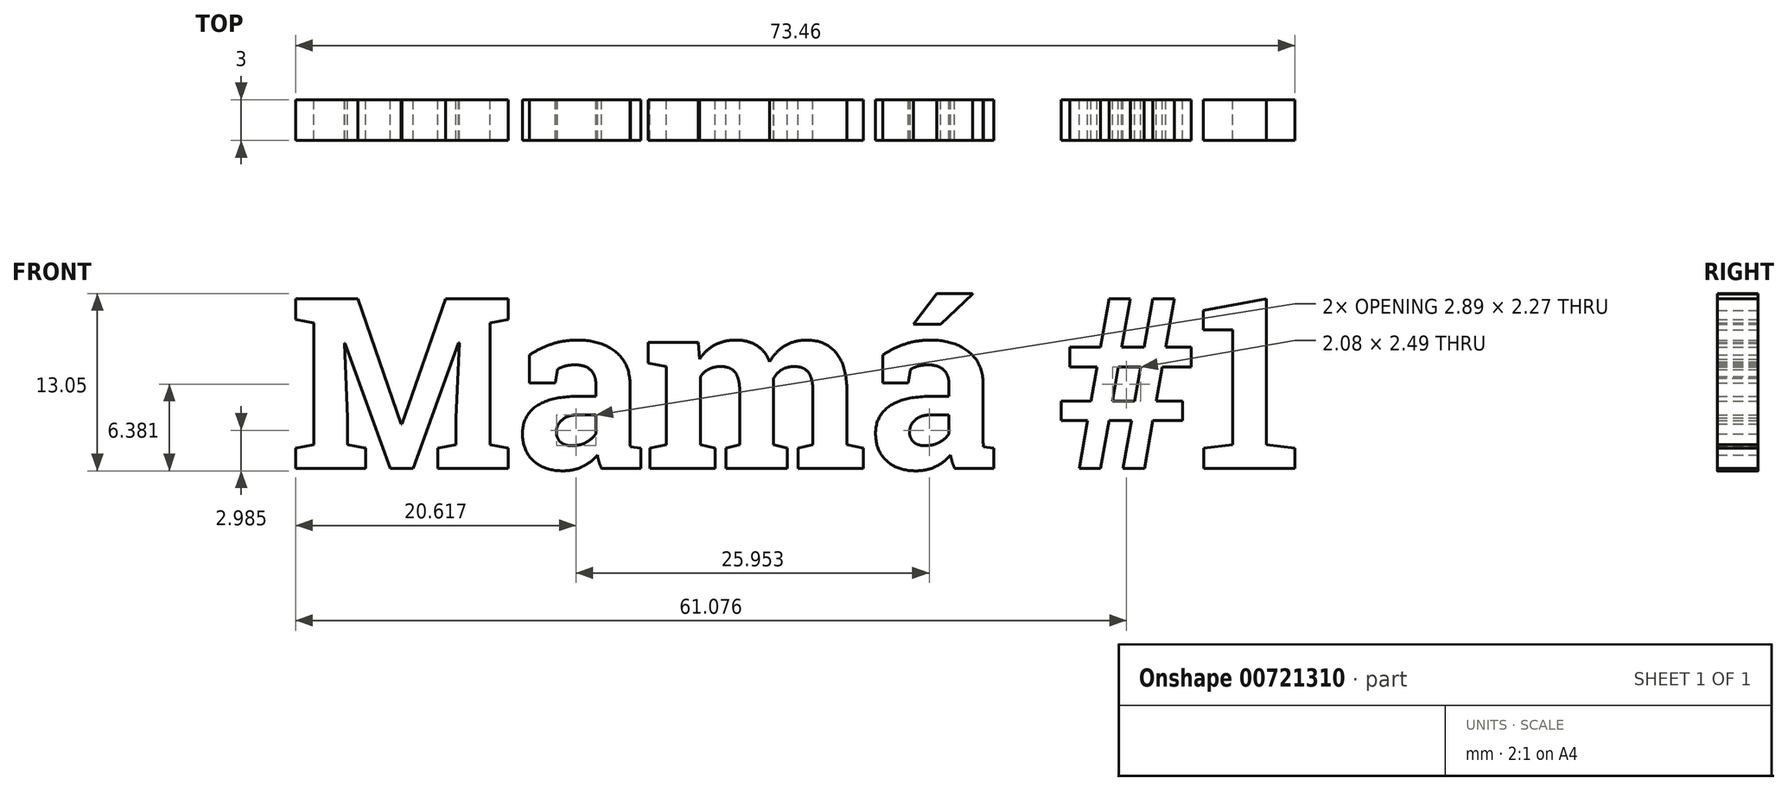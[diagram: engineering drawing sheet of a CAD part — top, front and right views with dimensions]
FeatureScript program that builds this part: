
annotation { "Feature Type Name" : "Feature", "Feature Type Description" : "" }
export const myFeature = defineFeature(function(context is Context, id is Id, definition is map)
    precondition{}
    {
        {
            var Q0;
            Q0=qCreatedBy(makeId("Front.planeOp"),FACE);
            var sketch = newSketch(context, id + "F0", { "sketchPlane" : qUnion([Q0])});
            skText(sketch, "E0", { "text": "Mamá #1", "fontName": "RobotoSlab-Bold.ttf"});
            const initialGuessF0  = {"E0": [-0.01059, 0.01373, 1, 0, 0.01263]};
            skSetInitialGuess(sketch, initialGuessF0);
            skSolve(sketch);
        }
        {
            var Q0;
            Q0 = qSketchRegion(id + "F0", true);
            extrude(context, id + "F1", {"entities" : qUnion([Q0]), "depth" : 3 * mm, "offsetDistance" : 25.4 * mm});
        }
    });
